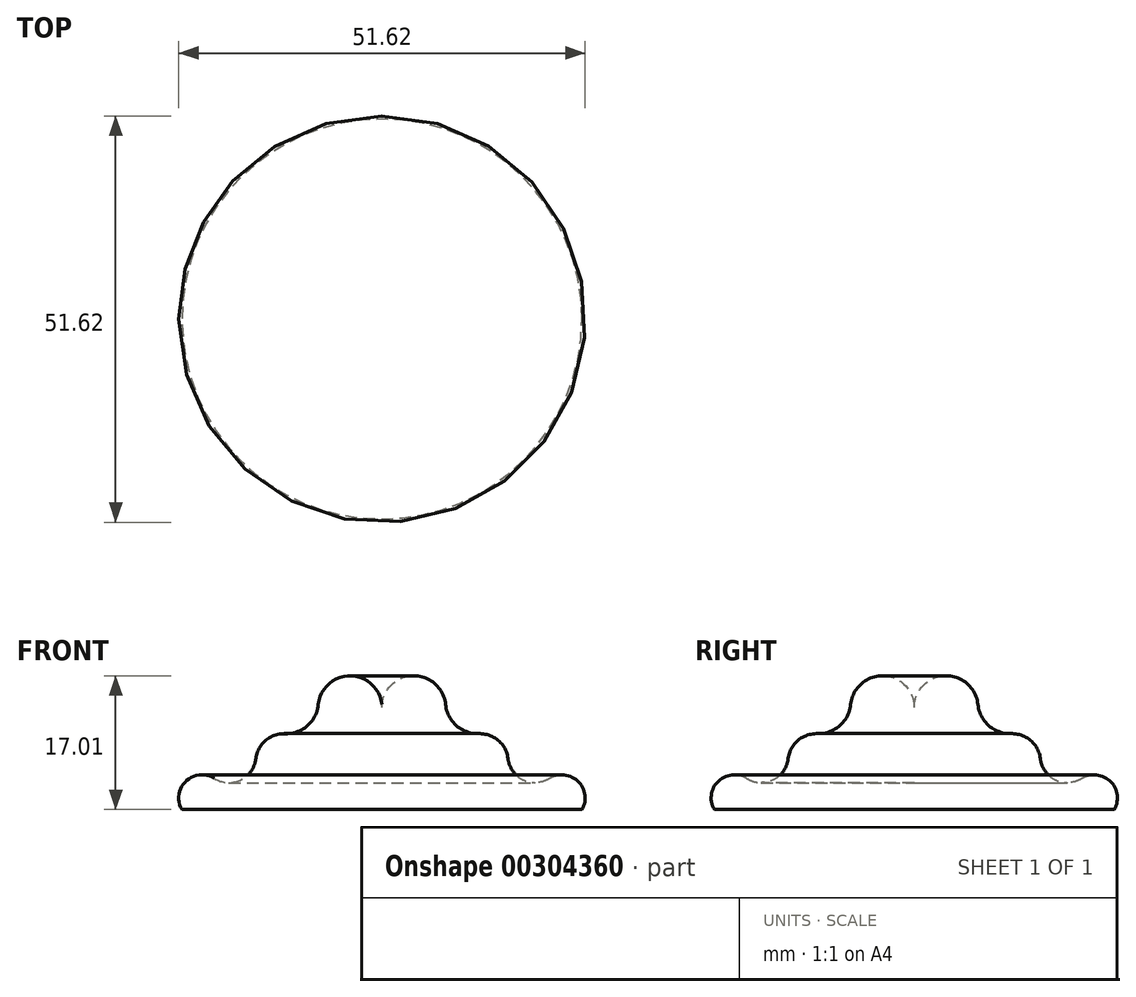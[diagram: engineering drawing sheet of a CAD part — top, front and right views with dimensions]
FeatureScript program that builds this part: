
annotation { "Feature Type Name" : "Feature", "Feature Type Description" : "" }
export const myFeature = defineFeature(function(context is Context, id is Id, definition is map)
    precondition{}
    {
        {
            var Q0;
            Q0=qCreatedBy(makeId("Front.planeOp"),FACE);
            var sketch = newSketch(context, id + "F0", { "sketchPlane" : qUnion([Q0])});
            skLineSegment(sketch, "E0", {"start": v(0, 0) * mm, "end": v(0, 12.95) * mm});
            skArc(sketch, "E1", {"start": v(0, 12.95) * mm, "mid": v(3.85, 17) * mm, "end": v(8.08, 13.35) * mm});
            skArc(sketch, "E2", {"start": v(8.08, 13.35) * mm, "mid": v(9.47, 10.66) * mm, "end": v(12.31, 9.65) * mm});
            skArc(sketch, "E3", {"start": v(12.31, 9.65) * mm, "mid": v(14.78, 8.78) * mm, "end": v(16.02, 6.48) * mm});
            skArc(sketch, "E4", {"start": v(16.02, 6.48) * mm, "mid": v(17.97, 3.76) * mm, "end": v(21.3, 3.97) * mm});
            skArc(sketch, "E5", {"start": v(21.3, 3.97) * mm, "mid": v(24.91, 3.6) * mm, "end": v(25.4, 0) * mm});
            skLineSegment(sketch, "E6", {"start": v(0, 0) * mm, "end": v(25.4, 0) * mm});
            skSolve(sketch);
        }
        {
            var Q0;
            Q0 = qSketchRegion(id + "F0", true);
            var Q1;
            Q1=sQuery(id+"F0.wireOp",EDGE,"E0");
            revolve(context, id + "F1", {"entities" : qUnion([Q0]), "axis" : qUnion([Q1]), "revolveType" : RevolveType.FULL});
        }
    });
